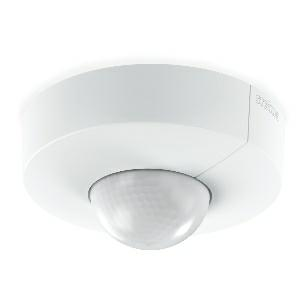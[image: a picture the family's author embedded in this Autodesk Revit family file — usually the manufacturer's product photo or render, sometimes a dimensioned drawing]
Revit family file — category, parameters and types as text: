
# Revit family: is_345_033798
name_source: partatom
category: Elektroinstallationen
revit_build: Autodesk Revit 2016 (Build: 20190508_0715(x64)
units: mm (PartAtom-declared; Revit-internal decimal feet)

## family parameters
Basisbauteil = Fläche
Beim Laden mit Abzugskörper schneiden = Nein
Bemaßung runder Anschluss = Durchmesser verwenden
Beschriftungsausrichtung beibehalten = Nein
Gemeinsam genutzt = Nein
Raumberechnungspunkt = Nein
Teiletyp = Normal

## types (1)
- IS 345
    Apparent Load = 0 VA
    Beschreibung = Type: Motion detectors; Dimensions (Ø x H): 126 x 65 mm; Mains power supply: 220 – 240 V / 50 – 60 Hz; Sensor Technology: passive infrared; Application, place: Outdoors, Indoors; Application, room: corridor / aisle, multi-storey / underground car park, outdoors, Indoors; Installation site: ceiling; Installation: Surface wiring; Switching zones: 280 switching zones; Electronic scalability: No; Mechanical scalability: No; Mounting height: 2,50 – 5,00 m; Optimum mounting height: 2,8 m; Detection angle: 360 °; Angle of aperture: 45 °; Sneak-by guard: Yes; Capability of masking out individual segments: Yes; Reach, radial: 12 x 6 m (72 m²); Reach, tangential: 23 x 6 m (138 m²); Twilight setting TEACH: Yes; Twilight setting: 2 – 1000 lx; Time setting: 5 sec – 15 min; Switching output 1, resistive: 2000 W; Switching output 1, number of LEDs / fluorescent lamps: 8 pcs.; Constant-lighting control: No; Basic light level function: No; Functions: Normal / test mode, Manual ON / ON-OFF; Settings via: Remote control, Potentiometers, Smart Remote; With remote control: No; Interconnection: Yes; IP-rating: IP54; Material: Plastic; Ambient temperature: -20 – 50 °C; Colour: white; Colour, RAL: 9003; Manufacturer's Warranty: 5 years; Version: COM1 - surface, rd.; PU1, EAN: 4007841033798
    Height = 0 mm  [stored 0 ft]
    Hersteller = Steinel
    Length = 126 mm
    Maximum range = 11.589 m
    ModVariant = Nein
    Modell = 033798
    Mounting Place = Ceiling
    Mounting Type = Surface mounted
    Number of Poles = 1
    OnlyDefault = Ja
    Power Factor = 1
    Product Name = IS 345
    Product group = Sensor-switched outdoor light
    ProductGroupID = 3
    Protection Class = Protection class
    Protection Degree = IP 54
    RlxData = <blob elided: 156189 chars, md5=d4ba1132>
    Sensor characteristics = Stretched
    Sensor type = Passive (infrared)
    SensorDataFile = <blob elided: 5885 chars, md5=98bccc25>
    Type of entry = Motion
    Typenbild = produkt1_033798.jpg
    Typenkommentare = Product without accessories
    URL = http://relux.com
    VarID = ---
    Voltage = 0 V
    Vorgabe-Ansicht = 1800 mm
    Weight = 0.00 kg
    Width = 0 mm  [stored 0 ft]

note: [stored X ft] marks values corroborated as IEEE doubles in the binary element streams (Revit-internal decimal feet)

## geometry (parser evidence)
native form markers: Blend x4, Sweep x18
no freeform markers — native parametric forms only
